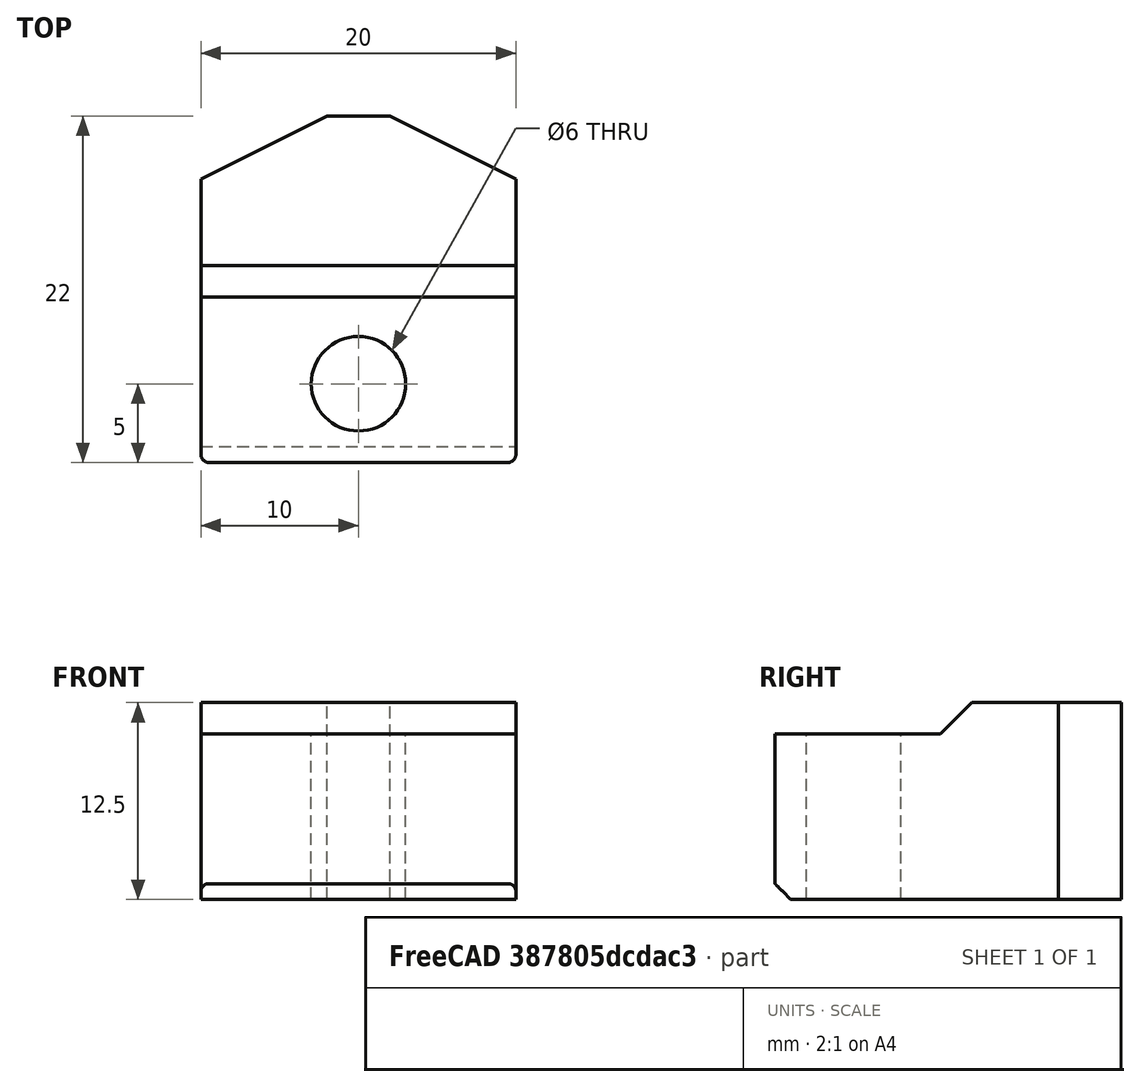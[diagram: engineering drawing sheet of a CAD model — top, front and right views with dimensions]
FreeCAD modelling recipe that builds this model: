
FCSTD DOCUMENT  (FreeCAD 0.18R16146 (Git))
Label: mello-heatblock
License: All rights reserved
LicenseURL: http://en.wikipedia.org/wiki/All_rights_reserved
objects: Part::Chamfer×3, Part::Box×2, Part::Cut×2, Part::Cylinder×1, Part::Fillet×1, Part::Feature×1
note: 10 computed .brp shape members not serialized (recipe doc carries the construction recipe); baked Part::Feature solids carry a one-line shape summary decoded from their .brp

FEATURE [Part::Box] Box  label="Cube"
  AttacherType = Attacher::AttachEngine3D
  Height = 12.5
  Length = 20
  Placement = pos=(-10,-4.5,0) rot=(0,0,1;0rad)
  Width = 22
FEATURE [Part::Cylinder] Cylinder
  Angle = 360
  AttacherType = Attacher::AttachEngine3D
  Height = 16
  Placement = pos=(0,0.5,0) rot=(0,0,1;0rad)
  Radius = 3
FEATURE [Part::Chamfer] Chamfer
  Base = -> Box
  Edges = 2 edges: [Edge3 r1=4 r2=8,Edge7 r1=4 r2=8]
FEATURE [Part::Chamfer] Chamfer001
  Base = -> Chamfer
  Edges = 1 edges r=1: [Edge12]
FEATURE [Part::Fillet] Fillet
  Base = -> Chamfer001
  Edges = 2 edges r=0.5: [Edge1,Edge6]
FEATURE [Part::Box] Box001  label="Cube001"
  AttacherType = Attacher::AttachEngine3D
  Height = 10
  Length = 21
  Placement = pos=(-10.5,-4.5,10.5) rot=(0,0,1;0rad)
  Width = 13
FEATURE [Part::Chamfer] Chamfer002
  Base = -> Box001
  Edges = 1 edges r=2.5: [Edge11]
FEATURE [Part::Cut] Cut
  Base = -> Fillet
  Tool = -> Cylinder
FEATURE [Part::Cut] Cut001
  Base = -> Cut
  Tool = -> Chamfer002
FEATURE [Part::Feature] Cut001001  label="heatblock-pref"
  shape: bbox 20 x 22 x 12.5 mm, 14 faces (baked)
